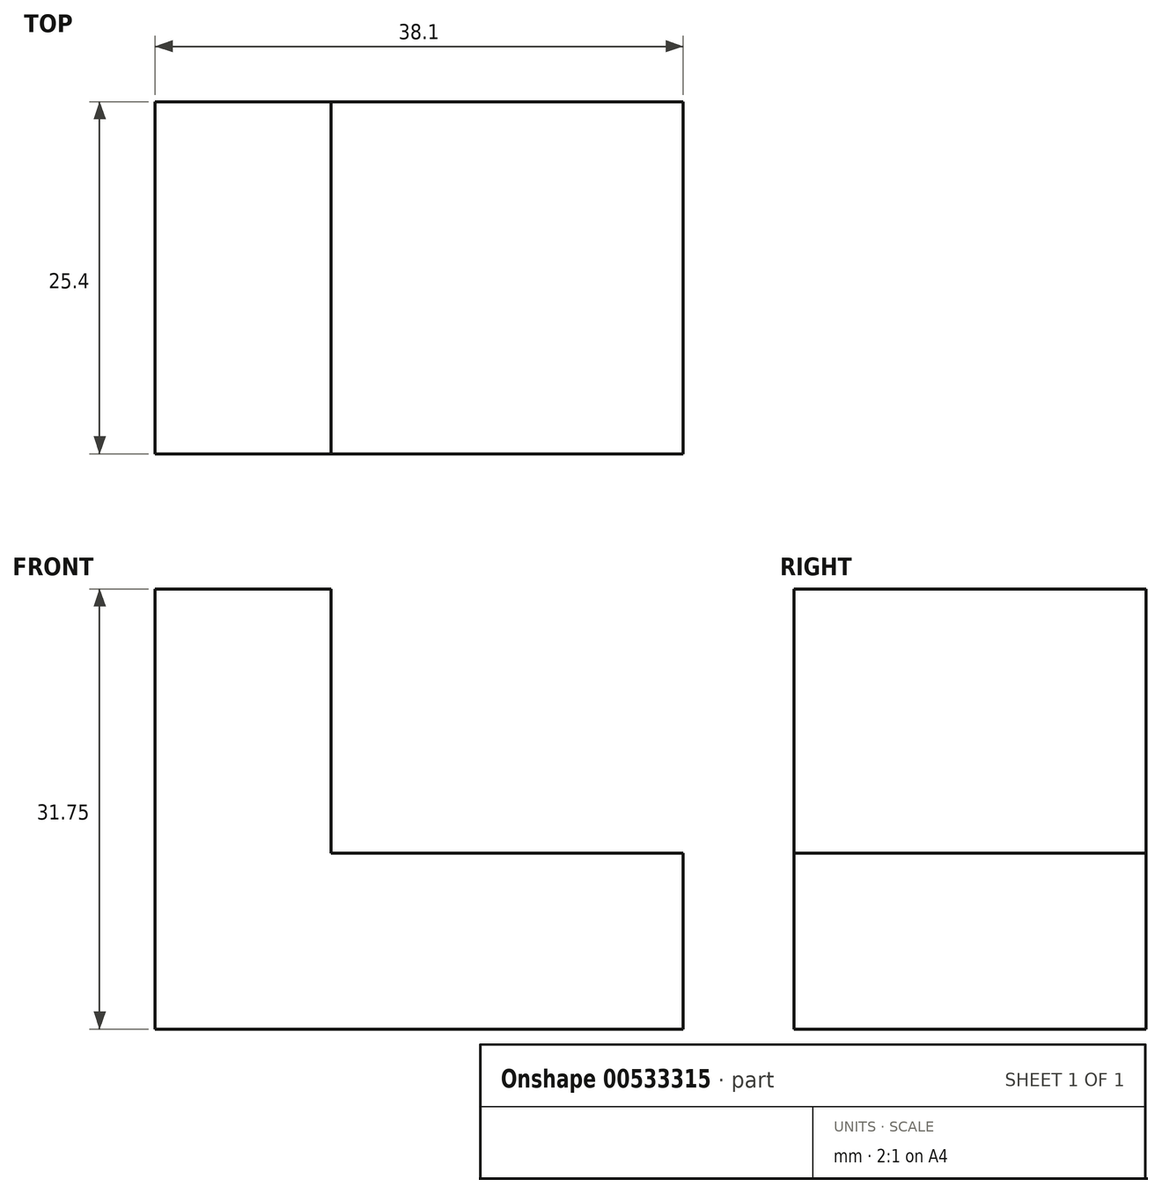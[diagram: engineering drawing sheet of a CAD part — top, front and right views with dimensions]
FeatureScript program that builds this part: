
annotation { "Feature Type Name" : "Feature", "Feature Type Description" : "" }
export const myFeature = defineFeature(function(context is Context, id is Id, definition is map)
    precondition{}
    {
        {
            var Q0;
            Q0=qCreatedBy(makeId("Front.planeOp"),FACE);
            var sketch = newSketch(context, id + "F0", { "sketchPlane" : qUnion([Q0])});
            skLineSegment(sketch, "E0", {"start": v(0, 0) * mm, "end": v(0, 31.75) * mm});
            skLineSegment(sketch, "E1", {"start": v(0, 31.75) * mm, "end": v(12.7, 31.75) * mm});
            skLineSegment(sketch, "E2", {"start": v(12.7, 31.75) * mm, "end": v(12.7, 12.7) * mm});
            skLineSegment(sketch, "E3", {"start": v(12.7, 12.7) * mm, "end": v(38.1, 12.7) * mm});
            skLineSegment(sketch, "E4", {"start": v(38.1, 12.7) * mm, "end": v(38.1, 0) * mm});
            skLineSegment(sketch, "E5", {"start": v(38.1, 0) * mm, "end": v(0, 0) * mm});
            skSolve(sketch);
        }
        {
            var Q0;
            Q0 = qSketchRegion(id + "F0", true);
            extrude(context, id + "F1", {"entities" : qUnion([Q0]), "oppositeDirection" : true, "depth" : 25.4 * mm, "offsetDistance" : 25.4 * mm});
        }
    });
